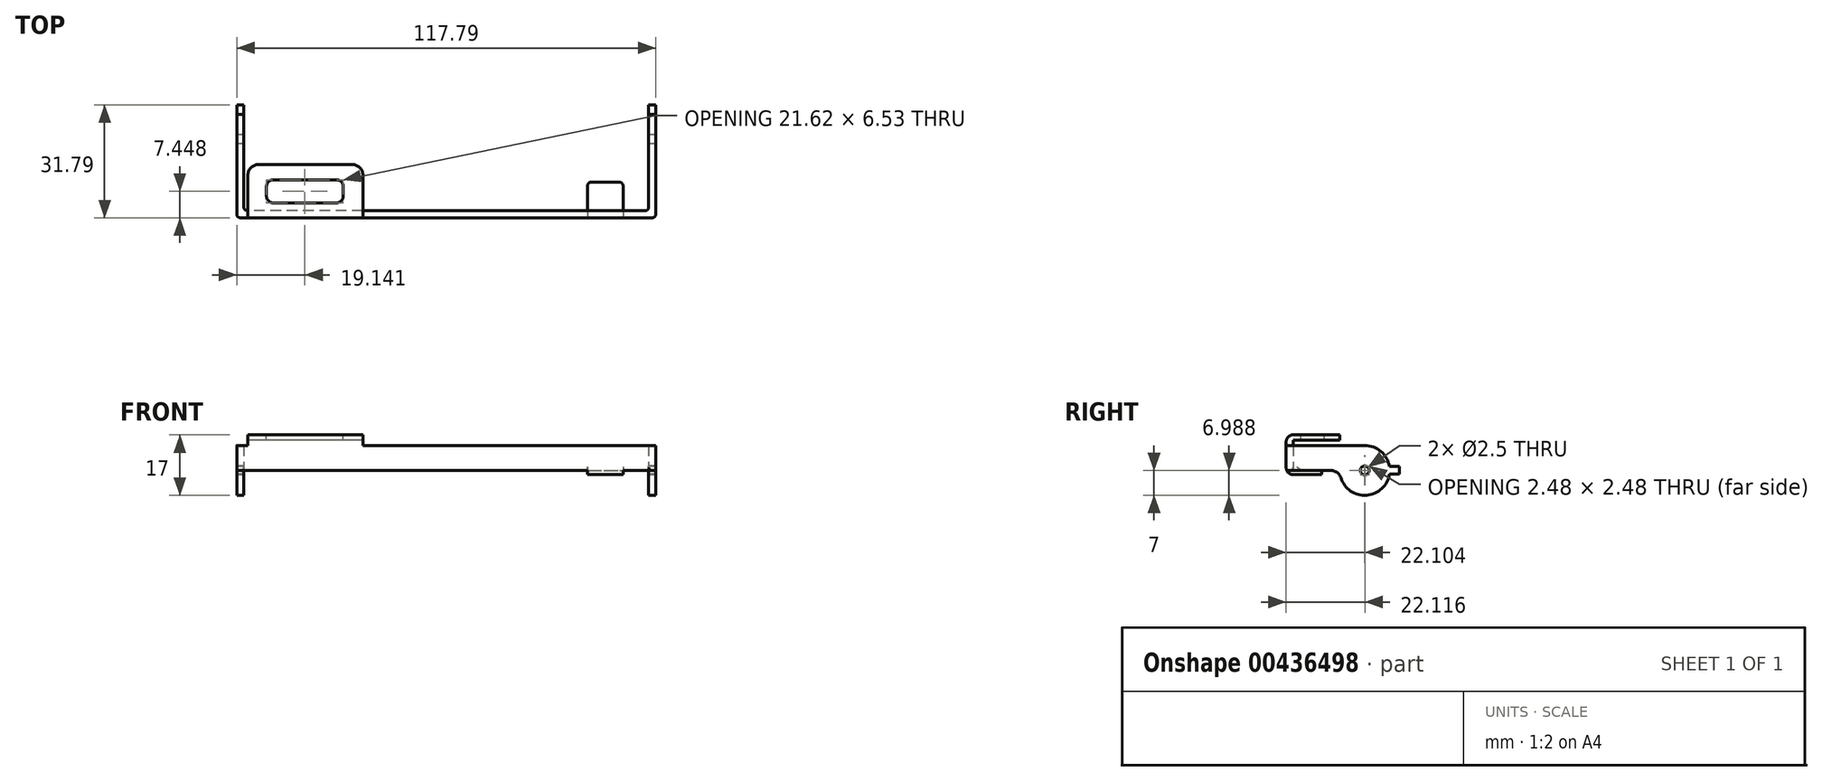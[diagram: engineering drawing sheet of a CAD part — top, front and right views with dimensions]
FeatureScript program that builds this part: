
annotation { "Feature Type Name" : "Feature", "Feature Type Description" : "" }
export const myFeature = defineFeature(function(context is Context, id is Id, definition is map)
    precondition{}
    {
        {
            var Q0;
            Q0=qCreatedBy(makeId("Top.planeOp"),FACE);
            var sketch = newSketch(context, id + "F0", { "sketchPlane" : qUnion([Q0])});
            skLineSegment(sketch, "E0.bottom", {"start": v(-116.8, 27.87) * mm, "end": v(-114.8, 27.87) * mm});
            skLineSegment(sketch, "E0.top", {"start": v(-116.8, -1.23) * mm, "end": v(0.99, -1.23) * mm});
            skLineSegment(sketch, "E0.left", {"start": v(-116.8, 27.87) * mm, "end": v(-116.8, -1.23) * mm});
            skLineSegment(sketch, "E0.right", {"start": v(0.99, 27.87) * mm, "end": v(0.99, -1.23) * mm});
            skLineSegment(sketch, "E1.1", {"start": v(-114.8, 0.77) * mm, "end": v(-1.01, 0.77) * mm});
            skLineSegment(sketch, "E1.2", {"start": v(-114.8, 27.87) * mm, "end": v(-114.8, 0.77) * mm});
            skLineSegment(sketch, "E2", {"start": v(0.99, 27.87) * mm, "end": v(-1.01, 27.87) * mm});
            skLineSegment(sketch, "E3", {"start": v(-1.01, 27.87) * mm, "end": v(-1.01, 0.77) * mm});
            skSolve(sketch);
        }
        {
            var Q0;
            Q0=makeQuery(id+"F0.imprint","IMPRINT",FACE,{"disambiguationData":[TD([[makeQuery(id+"F0.imprint","IMPRINT",EDGE,{"derivedFrom":sQuery(id+"F0.wireOp",EDGE,"E0.bottom")}),-1.0]])]});
            extrude(context, id + "F1", {"entities" : qUnion([Q0]), "depth" : 7 * mm});
        }
        {
            var Q0;
            Q0=makeQuery(id+"F1.opExtrude","SWEPT_FACE",FACE,{"disambiguationData":[OSD([sQuery(id+"F0.wireOp",EDGE,"E0.left")])]});
            var sketch = newSketch(context, id + "F2", { "sketchPlane" : qUnion([Q0])});
            skCircle(sketch, "E4", {"center": v(-20.87, 0) * mm, "radius": 7 * mm});
            skSolve(sketch);
        }
        {
            var Q0;
            Q0 = qSketchRegion(id + "F2", true);
            extrude(context, id + "F3", {"entities" : qUnion([Q0]), "operationType" : NewBodyOperationType.ADD, "oppositeDirection" : true, "depth" : 2 * mm});
        }
        {
            var Q0;
            Q0=makeQuery(id+"F1.opExtrude","SWEPT_FACE",FACE,{"disambiguationData":[OSD([sQuery(id+"F0.wireOp",EDGE,"E3")])]});
            var sketch = newSketch(context, id + "F4", { "sketchPlane" : qUnion([Q0])});
            skCircle(sketch, "E5.0", {"center": v(-20.87, 0) * mm, "radius": 7 * mm});
            skSolve(sketch);
        }
        {
            var Q0;
            Q0 = qSketchRegion(id + "F4", true);
            extrude(context, id + "F5", {"entities" : qUnion([Q0]), "operationType" : NewBodyOperationType.ADD, "oppositeDirection" : true, "depth" : 2 * mm});
        }
        {
            var Q0;
            {var subQ2=sQuery(id+"F0.wireOp",EDGE,"E0.right");var subQ5=sQuery(id+"F0.wireOp",EDGE,"E0.left");var subQ7=sQuery(id+"F0.wireOp",EDGE,"E3");var subQ9=sQuery(id+"F0.wireOp",EDGE,"E1.2");var subQ12=sQuery(id+"F0.wireOp",EDGE,"E1.1");var subQ14=sQuery(id+"F0.wireOp",EDGE,"E0.top");var subQ15=makeQuery(id+"F1.opExtrude","SWEPT_FACE",FACE,{"disambiguationData":[OSD([subQ14])]});var subQ17=sQuery(id+"F0.wireOp",EDGE,"E2");Q0=makeQuery(id+"F5.boolean.opBoolean","SPLIT",FACE,{"disambiguationData":[TD([subQ15])],"derivedFrom":makeQuery(id+"F3.boolean.opBoolean","SPLIT",FACE,{"disambiguationData":[TD([subQ15])],"derivedFrom":makeQuery(id+"F1.opExtrude","CAP_FACE",FACE,{"disambiguationData":[OSD([sQuery(id+"F0.wireOp",EDGE,"E0.bottom"),subQ14,subQ5,subQ2,subQ12,subQ9,subQ17,subQ7])],"isStart":false})})});}
            var sketch = newSketch(context, id + "F6", { "sketchPlane" : qUnion([Q0])});
            skLineSegment(sketch, "E6.bottom", {"start": v(-113.67, 0.77) * mm, "end": v(-81.36, 0.77) * mm});
            skLineSegment(sketch, "E6.top", {"start": v(-113.67, -1.23) * mm, "end": v(-81.36, -1.23) * mm});
            skLineSegment(sketch, "E6.left", {"start": v(-113.67, 0.77) * mm, "end": v(-113.67, -1.23) * mm});
            skLineSegment(sketch, "E6.right", {"start": v(-81.36, 0.77) * mm, "end": v(-81.36, -1.23) * mm});
            skSolve(sketch);
        }
        {
            var Q0;
            Q0 = qSketchRegion(id + "F6", true);
            extrude(context, id + "F7", {"entities" : qUnion([Q0]), "operationType" : NewBodyOperationType.ADD, "depth" : 3 * mm});
        }
        {
            var Q0;
            Q0=makeQuery(id+"F7.boolean.opBoolean","MERGE",FACE,{"derivedFrom":[makeQuery(id+"F1.opExtrude","SWEPT_FACE",FACE,{"disambiguationData":[OSD([sQuery(id+"F0.wireOp",EDGE,"E1.1")])]}),makeQuery(id+"F7.opExtrude","SWEPT_FACE",FACE,{"disambiguationData":[OSD([sQuery(id+"F6.wireOp",EDGE,"E6.bottom")])]})]});
            var sketch = newSketch(context, id + "F8", { "sketchPlane" : qUnion([Q0])});
            skLineSegment(sketch, "E7.bottom", {"start": v(81.36, 10) * mm, "end": v(113.67, 10) * mm});
            skLineSegment(sketch, "E7.top", {"start": v(81.36, 8.5) * mm, "end": v(113.67, 8.5) * mm});
            skLineSegment(sketch, "E7.left", {"start": v(81.36, 10) * mm, "end": v(81.36, 8.5) * mm});
            skLineSegment(sketch, "E7.right", {"start": v(113.67, 10) * mm, "end": v(113.67, 8.5) * mm});
            skSolve(sketch);
        }
        {
            var Q0;
            Q0 = qSketchRegion(id + "F8", true);
            extrude(context, id + "F9", {"entities" : qUnion([Q0]), "operationType" : NewBodyOperationType.ADD, "depth" : 13 * mm});
        }
        {
            var Q0;
            Q0=makeQuery(id+"F9.boolean.opBoolean","MERGE",FACE,{"derivedFrom":[makeQuery(id+"F7.opExtrude","CAP_FACE",FACE,{"disambiguationData":[OSD([sQuery(id+"F6.wireOp",EDGE,"E6.bottom"),sQuery(id+"F6.wireOp",EDGE,"E6.top"),sQuery(id+"F6.wireOp",EDGE,"E6.left"),sQuery(id+"F6.wireOp",EDGE,"E6.right")])],"isStart":false}),makeQuery(id+"F9.opExtrude","SWEPT_FACE",FACE,{"disambiguationData":[OSD([sQuery(id+"F8.wireOp",EDGE,"E7.bottom")])]})]});
            var sketch = newSketch(context, id + "F10", { "sketchPlane" : qUnion([Q0])});
            skLineSegment(sketch, "E8.bottom", {"start": v(-88.85, 9.48) * mm, "end": v(-106.47, 9.48) * mm});
            skLineSegment(sketch, "E8.top", {"start": v(-88.85, 2.95) * mm, "end": v(-106.47, 2.95) * mm});
            skLineSegment(sketch, "E8.left", {"start": v(-86.85, 7.48) * mm, "end": v(-86.85, 4.95) * mm});
            skLineSegment(sketch, "E8.right", {"start": v(-108.47, 7.48) * mm, "end": v(-108.47, 4.95) * mm});
            skPoint(sketch, "E9.visualSharp", {"position": v(-86.85, 9.48) * mm});
            skArc(sketch, "E9.filletArc", {"start": v(-86.85, 7.48) * mm, "mid": v(-87.43, 8.9) * mm, "end": v(-88.85, 9.48) * mm});
            skPoint(sketch, "E10.visualSharp", {"position": v(-86.85, 2.95) * mm});
            skArc(sketch, "E10.filletArc", {"start": v(-88.85, 2.95) * mm, "mid": v(-87.43, 3.54) * mm, "end": v(-86.85, 4.95) * mm});
            skPoint(sketch, "E11.visualSharp", {"position": v(-108.47, 2.95) * mm});
            skArc(sketch, "E11.filletArc", {"start": v(-108.27, 4.07) * mm, "mid": v(-107.94, 3.6) * mm, "end": v(-107.49, 3.23) * mm});
            skPoint(sketch, "E12.visualSharp", {"position": v(-108.47, 9.48) * mm});
            skArc(sketch, "E12.filletArc", {"start": v(-106.47, 9.48) * mm, "mid": v(-107.88, 8.9) * mm, "end": v(-108.47, 7.48) * mm});
            skArc(sketch, "E13.filletArc", {"start": v(-108.47, 4.95) * mm, "mid": v(-107.88, 3.54) * mm, "end": v(-106.47, 2.95) * mm});
            skSolve(sketch);
        }
        {
            var Q0;
            Q0=makeQuery(id+"F7.boolean.opBoolean","MERGE",FACE,{"derivedFrom":[makeQuery(id+"F1.opExtrude","SWEPT_FACE",FACE,{"disambiguationData":[OSD([sQuery(id+"F0.wireOp",EDGE,"E0.top")])]}),makeQuery(id+"F7.opExtrude","SWEPT_FACE",FACE,{"disambiguationData":[OSD([sQuery(id+"F6.wireOp",EDGE,"E6.top")])]})]});
            var sketch = newSketch(context, id + "F11", { "sketchPlane" : qUnion([Q0])});
            skLineSegment(sketch, "E14.bottom", {"start": v(-8.21, 0) * mm, "end": v(-18.21, 0) * mm});
            skLineSegment(sketch, "E14.top", {"start": v(-8.21, -1.2) * mm, "end": v(-18.21, -1.2) * mm});
            skLineSegment(sketch, "E14.left", {"start": v(-8.21, 0) * mm, "end": v(-8.21, -1.2) * mm});
            skLineSegment(sketch, "E14.right", {"start": v(-18.21, 0) * mm, "end": v(-18.21, -1.2) * mm});
            skSolve(sketch);
        }
        {
            var Q0;
            Q0=makeQuery(id+"F11.imprint","IMPRINT",FACE,{"disambiguationData":[TD([[makeQuery(id+"F11.imprint","IMPRINT",EDGE,{"derivedFrom":sQuery(id+"F11.wireOp",EDGE,"E14.bottom")}),-1.0]])]});
            extrude(context, id + "F12", {"entities" : qUnion([Q0]), "operationType" : NewBodyOperationType.ADD, "oppositeDirection" : true, "depth" : 10 * mm});
        }
        {
            var Q0;
            Q0=makeQuery(id+"F10.imprint","IMPRINT",FACE,{"disambiguationData":[TD([[makeQuery(id+"F10.imprint","IMPRINT",EDGE,{"derivedFrom":sQuery(id+"F10.wireOp",EDGE,"E8.bottom")}),1.0]])]});
            extrude(context, id + "F13", {"entities" : qUnion([Q0]), "operationType" : NewBodyOperationType.REMOVE, "oppositeDirection" : true, "depth" : 25 * mm});
        }
        {
            var Q0;
            Q0=makeQuery(id+"F9.opExtrude","CAP_EDGE",EDGE,{"disambiguationData":[OSD([sQuery(id+"F8.wireOp",EDGE,"E7.right")])],"isStart":false});
            var Q1;
            Q1=makeQuery(id+"F9.opExtrude","CAP_EDGE",EDGE,{"disambiguationData":[OSD([sQuery(id+"F8.wireOp",EDGE,"E7.left")])],"isStart":false});
            fillet(context, id + "F14", {"entities" : qUnion([Q0, Q1]), "radius" : 3 * mm, "tangentPropagation" : true, "allowEdgeOverflow" : false});
        }
        {
            var Q0;
            Q0=makeQuery(id+"F7.opExtrude","CAP_EDGE",EDGE,{"disambiguationData":[OSD([sQuery(id+"F6.wireOp",EDGE,"E6.top")])],"isStart":false});
            var Q1;
            Q1=makeQuery(id+"F9.opExtrude","CAP_EDGE",EDGE,{"disambiguationData":[OSD([sQuery(id+"F8.wireOp",EDGE,"E7.top")])],"isStart":true});
            var Q2;
            Q2=makeQuery(id+"F12.opExtrude","CAP_EDGE",EDGE,{"disambiguationData":[OSD([sQuery(id+"F11.wireOp",EDGE,"E14.top")])],"isStart":true});
            fillet(context, id + "F15", {"entities" : qUnion([Q0, Q1, Q2]), "radius" : 2 * mm, "tangentPropagation" : true, "allowEdgeOverflow" : false});
        }
        {
            var Q0;
            {var subQ0=sQuery(id+"F0.wireOp",EDGE,"E1.1");Q0=makeQuery(id+"F12.boolean.opBoolean","SPLIT",EDGE,{"disambiguationData":[topologyDisambiguationEdgeConnected([makeQuery(id+"F1.opExtrude","SWEPT_FACE",FACE,{"disambiguationData":[OSD([subQ0])]}),makeQuery(id+"F7.opExtrude","SWEPT_FACE",FACE,{"disambiguationData":[OSD([sQuery(id+"F6.wireOp",EDGE,"E6.bottom")])]}),makeQuery(id+"F12.opExtrude","SWEPT_FACE",FACE,{"disambiguationData":[OSD([sQuery(id+"F11.wireOp",EDGE,"E14.bottom")])]})])],"derivedFrom":makeQuery(id+"F1.opExtrude","CAP_EDGE",EDGE,{"disambiguationData":[OSD([subQ0])],"isStart":true})});}
            var Q1;
            Q1=makeQuery(id+"F1.opExtrude","SWEPT_EDGE",EDGE,{"disambiguationData":[OSD([sQuery(id+"F0.wireOp",EDGE,"E1.1"),sQuery(id+"F0.wireOp",EDGE,"E3")])]});
            var Q2;
            Q2=makeQuery(id+"F1.opExtrude","SWEPT_EDGE",EDGE,{"disambiguationData":[OSD([sQuery(id+"F0.wireOp",EDGE,"E0.top"),sQuery(id+"F0.wireOp",EDGE,"E0.right")])]});
            var Q3;
            Q3=makeQuery(id+"F1.opExtrude","SWEPT_EDGE",EDGE,{"disambiguationData":[OSD([sQuery(id+"F0.wireOp",EDGE,"E0.top"),sQuery(id+"F0.wireOp",EDGE,"E0.left")])]});
            var Q4;
            Q4=makeQuery(id+"F1.opExtrude","SWEPT_EDGE",EDGE,{"disambiguationData":[OSD([sQuery(id+"F0.wireOp",EDGE,"E1.1"),sQuery(id+"F0.wireOp",EDGE,"E1.2")])]});
            var Q5;
            Q5=makeQuery(id+"F12.opExtrude","CAP_EDGE",EDGE,{"disambiguationData":[OSD([sQuery(id+"F11.wireOp",EDGE,"E14.right")])],"isStart":false});
            var Q6;
            Q6=makeQuery(id+"F12.opExtrude","CAP_EDGE",EDGE,{"disambiguationData":[OSD([sQuery(id+"F11.wireOp",EDGE,"E14.left")])],"isStart":false});
            fillet(context, id + "F16", {"entities" : qUnion([Q0, Q1, Q2, Q3, Q4, Q5, Q6]), "radius" : 1 * mm, "tangentPropagation" : true, "allowEdgeOverflow" : false});
        }
        {
            var Q0;
            {var subQ1=sQuery(id+"F0.wireOp",EDGE,"E0.left");var subQ2=makeQuery(id+"F1.opExtrude","SWEPT_EDGE",EDGE,{"disambiguationData":[OSD([sQuery(id+"F0.wireOp",EDGE,"E0.bottom"),subQ1])]});Q0=makeQuery(id+"F2.imprint","IMPRINT",FACE,{"disambiguationData":[TD([[makeQuery(id+"F2.imprint","IMPRINT",EDGE,{"derivedFrom":subQ2}),1.0]])]});}
            extrude(context, id + "F17", {"entities" : qUnion([Q0]), "operationType" : NewBodyOperationType.REMOVE, "endBound" : BoundingType.THROUGH_ALL, "oppositeDirection" : true, "depth" : 25 * mm});
        }
        {
            var Q0;
            Q0=makeQuery(id+"F3.boolean.opBoolean","INTERSECT",EDGE,{"derivedFrom":[makeQuery(id+"F1.opExtrude","CAP_FACE",FACE,{"disambiguationData":[OSD([sQuery(id+"F0.wireOp",EDGE,"E0.bottom"),sQuery(id+"F0.wireOp",EDGE,"E0.top"),sQuery(id+"F0.wireOp",EDGE,"E0.left"),sQuery(id+"F0.wireOp",EDGE,"E0.right"),sQuery(id+"F0.wireOp",EDGE,"E1.1"),sQuery(id+"F0.wireOp",EDGE,"E1.2"),sQuery(id+"F0.wireOp",EDGE,"E2"),sQuery(id+"F0.wireOp",EDGE,"E3")])],"isStart":true}),makeQuery(id+"F3.opExtrude","SWEPT_FACE",FACE,{"disambiguationData":[OSD([sQuery(id+"F2.wireOp",EDGE,"E4")])]})]});
            var Q1;
            Q1=makeQuery(id+"F5.boolean.opBoolean","INTERSECT",EDGE,{"derivedFrom":[makeQuery(id+"F1.opExtrude","CAP_FACE",FACE,{"disambiguationData":[OSD([sQuery(id+"F0.wireOp",EDGE,"E0.bottom"),sQuery(id+"F0.wireOp",EDGE,"E0.top"),sQuery(id+"F0.wireOp",EDGE,"E0.left"),sQuery(id+"F0.wireOp",EDGE,"E0.right"),sQuery(id+"F0.wireOp",EDGE,"E1.1"),sQuery(id+"F0.wireOp",EDGE,"E1.2"),sQuery(id+"F0.wireOp",EDGE,"E2"),sQuery(id+"F0.wireOp",EDGE,"E3")])],"isStart":true}),makeQuery(id+"F5.opExtrude","SWEPT_FACE",FACE,{"disambiguationData":[OSD([sQuery(id+"F4.wireOp",EDGE,"E5.0")])]})]});
            fillet(context, id + "F18", {"entities" : qUnion([Q0, Q1]), "radius" : 3 * mm, "tangentPropagation" : true, "allowEdgeOverflow" : false});
        }
        {
            var Q0;
            {var subQ0=sQuery(id+"F2.wireOp",EDGE,"E4");var subQ1=sQuery(id+"F0.wireOp",EDGE,"E0.left");var subQ2=makeQuery(id+"F1.opExtrude","CAP_EDGE",EDGE,{"disambiguationData":[OSD([subQ1])],"isStart":true});var subQ4=makeQuery(id+"F2.imprint","INTERSECT",VERTEX,{"derivedFrom":[subQ2,subQ0]});Q0=makeQuery(id+"F2.imprint","IMPRINT",FACE,{"disambiguationData":[TD([[makeQuery(id+"F2.imprint","IMPRINT",EDGE,{"disambiguationData":[TD([[subQ4,1.0]])],"derivedFrom":subQ0}),1.0]])]});}
            var sketch = newSketch(context, id + "F19", { "sketchPlane" : qUnion([Q0])});
            skLineSegment(sketch, "E15.bottom", {"start": v(-30.56, 1.08) * mm, "end": v(-25.52, 1.08) * mm});
            skLineSegment(sketch, "E15.top", {"start": v(-30.56, -1.08) * mm, "end": v(-25.52, -1.08) * mm});
            skLineSegment(sketch, "E15.left", {"start": v(-30.56, 1.08) * mm, "end": v(-30.56, -1.08) * mm});
            skLineSegment(sketch, "E15.right", {"start": v(-25.52, 1.08) * mm, "end": v(-25.52, -1.08) * mm});
            skPoint(sketch, "E15.middle", {"position": v(-28.04, 0) * mm});
            skSolve(sketch);
        }
        {
            var Q0;
            Q0 = qSketchRegion(id + "F19", true);
            extrude(context, id + "F20", {"entities" : qUnion([Q0]), "operationType" : NewBodyOperationType.ADD, "oppositeDirection" : true, "depth" : 2 * mm});
        }
        {
            var Q0;
            Q0=makeQuery(id+"F5.boolean.opBoolean","MERGE",FACE,{"derivedFrom":[makeQuery(id+"F1.opExtrude","SWEPT_FACE",FACE,{"disambiguationData":[OSD([sQuery(id+"F0.wireOp",EDGE,"E3")])]}),makeQuery(id+"F5.opExtrude","CAP_FACE",FACE,{"disambiguationData":[OSD([sQuery(id+"F4.wireOp",EDGE,"E5.0")])],"isStart":true})]});
            var sketch = newSketch(context, id + "F21", { "sketchPlane" : qUnion([Q0])});
            skLineSegment(sketch, "E16.0", {"start": v(-30.56, 1.08) * mm, "end": v(-25.52, 1.08) * mm});
            skLineSegment(sketch, "E16.1", {"start": v(-25.52, 1.08) * mm, "end": v(-25.52, -1.08) * mm});
            skLineSegment(sketch, "E16.2", {"start": v(-30.56, -1.08) * mm, "end": v(-25.52, -1.08) * mm});
            skLineSegment(sketch, "E16.3", {"start": v(-30.56, 1.08) * mm, "end": v(-30.56, -1.08) * mm});
            skSolve(sketch);
        }
        {
            var Q0;
            {var subQ0=sQuery(id+"F21.wireOp",EDGE,"E16.3");Q0=makeQuery(id+"F21.imprint","IMPRINT",FACE,{"disambiguationData":[TD([[makeQuery(id+"F21.imprint","IMPRINT",EDGE,{"derivedFrom":subQ0}),1.0]])]});}
            extrude(context, id + "F22", {"entities" : qUnion([Q0]), "operationType" : NewBodyOperationType.ADD, "oppositeDirection" : true, "depth" : 2 * mm});
        }
        {
            var Q0;
            Q0=sQuery(id+"F2.wireOp",VERTEX,"E4.center");
            var Q1;
            Q1=makeQuery(id+"F1.opExtrude","SWEPT_BODY",BODY,{"disambiguationData":[OSD([sQuery(id+"F0.wireOp",EDGE,"E0.bottom"),sQuery(id+"F0.wireOp",EDGE,"E0.top"),sQuery(id+"F0.wireOp",EDGE,"E0.left"),sQuery(id+"F0.wireOp",EDGE,"E0.right"),sQuery(id+"F0.wireOp",EDGE,"E1.1"),sQuery(id+"F0.wireOp",EDGE,"E1.2"),sQuery(id+"F0.wireOp",EDGE,"E2"),sQuery(id+"F0.wireOp",EDGE,"E3")])]});
            hole(context, id + "F23", {"style" : HoleStyle.SIMPLE, "endStyle" : HoleEndStyle.THROUGH, "holeDiameter" : 2.5 * mm, "isTappedThrough" : true, "tappedDepth" : 12 * mm, "tapClearance" : 3, "locations" : qUnion([Q0]), "scope" : qUnion([Q1])});
        }
    });
